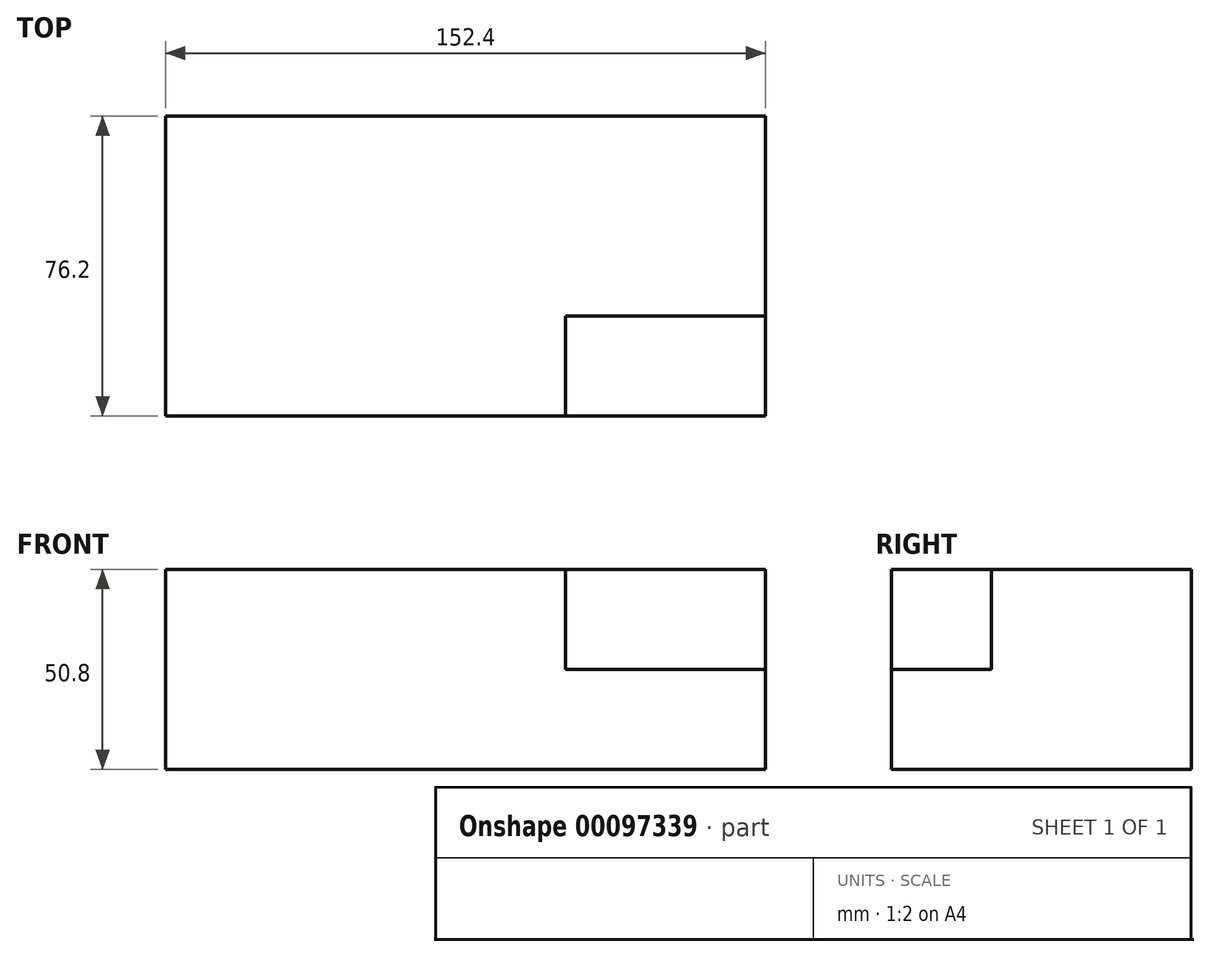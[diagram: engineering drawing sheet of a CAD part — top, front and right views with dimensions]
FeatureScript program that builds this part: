
annotation { "Feature Type Name" : "Feature", "Feature Type Description" : "" }
export const myFeature = defineFeature(function(context is Context, id is Id, definition is map)
    precondition{}
    {
        {
            var Q0;
            Q0=qCreatedBy(makeId("Front.planeOp"),FACE);
            var sketch = newSketch(context, id + "F0", { "sketchPlane" : qUnion([Q0])});
            skLineSegment(sketch, "E0.bottom", {"start": v(0, 0) * mm, "end": v(152.4, 0) * mm});
            skLineSegment(sketch, "E0.top", {"start": v(0, 50.8) * mm, "end": v(152.4, 50.8) * mm});
            skLineSegment(sketch, "E0.left", {"start": v(0, 0) * mm, "end": v(0, 50.8) * mm});
            skLineSegment(sketch, "E0.right", {"start": v(152.4, 0) * mm, "end": v(152.4, 50.8) * mm});
            skSolve(sketch);
        }
        {
            var Q0;
            Q0=makeQuery(id+"F0.imprint","IMPRINT",FACE,{"disambiguationData":[TD([[makeQuery(id+"F0.imprint","IMPRINT",EDGE,{"derivedFrom":sQuery(id+"F0.wireOp",EDGE,"E0.bottom")}),1.0]])]});
            extrude(context, id + "F1", {"entities" : qUnion([Q0]), "depth" : 76.2 * mm, "symmetric" : true});
        }
        {
            var Q0;
            Q0=makeQuery(id+"F1.opExtrude","SWEPT_FACE",FACE,{"disambiguationData":[OSD([sQuery(id+"F0.wireOp",EDGE,"E0.right")])]});
            var sketch = newSketch(context, id + "F2", { "sketchPlane" : qUnion([Q0])});
            skLineSegment(sketch, "E1.bottom", {"start": v(-38.1, 50.8) * mm, "end": v(-12.7, 50.8) * mm});
            skLineSegment(sketch, "E1.top", {"start": v(-38.1, 25.4) * mm, "end": v(-12.7, 25.4) * mm});
            skLineSegment(sketch, "E1.left", {"start": v(-38.1, 50.8) * mm, "end": v(-38.1, 25.4) * mm});
            skLineSegment(sketch, "E1.right", {"start": v(-12.7, 50.8) * mm, "end": v(-12.7, 25.4) * mm});
            skSolve(sketch);
        }
        {
            var Q0;
            Q0=makeQuery(id+"F2.imprint","IMPRINT",FACE,{"disambiguationData":[TD([[makeQuery(id+"F2.imprint","IMPRINT",EDGE,{"derivedFrom":sQuery(id+"F2.wireOp",EDGE,"E1.bottom")}),-1.0]])]});
            extrude(context, id + "F3", {"entities" : qUnion([Q0]), "operationType" : NewBodyOperationType.REMOVE, "oppositeDirection" : true, "depth" : 50.8 * mm});
        }
    });
